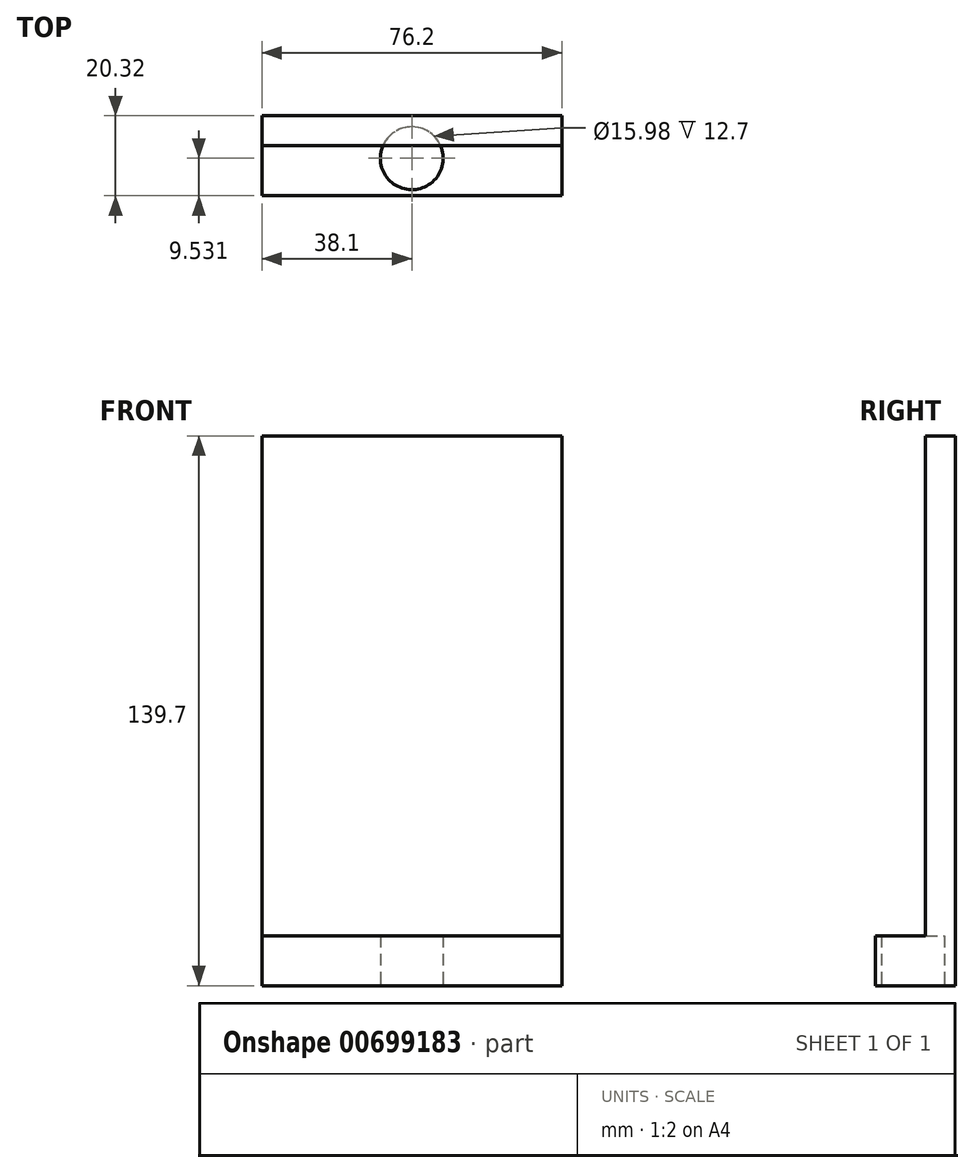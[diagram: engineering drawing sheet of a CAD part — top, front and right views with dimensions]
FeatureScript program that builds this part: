
annotation { "Feature Type Name" : "Feature", "Feature Type Description" : "" }
export const myFeature = defineFeature(function(context is Context, id is Id, definition is map)
    precondition{}
    {
        {
            var Q0;
            Q0=qCreatedBy(makeId("Front.planeOp"),FACE);
            var sketch = newSketch(context, id + "F0", { "sketchPlane" : qUnion([Q0])});
            skLineSegment(sketch, "E0.bottom", {"start": v(-38.1, 69.85) * mm, "end": v(38.1, 69.85) * mm});
            skLineSegment(sketch, "E0.top", {"start": v(-38.1, -69.85) * mm, "end": v(38.1, -69.85) * mm});
            skLineSegment(sketch, "E0.left", {"start": v(-38.1, 69.85) * mm, "end": v(-38.1, -69.85) * mm});
            skLineSegment(sketch, "E0.right", {"start": v(38.1, 69.85) * mm, "end": v(38.1, -69.85) * mm});
            skPoint(sketch, "E0.middle", {"position": v(0, 0) * mm});
            skSolve(sketch);
        }
        {
            var Q0;
            Q0 = qSketchRegion(id + "F0", true);
            extrude(context, id + "F1", {"entities" : qUnion([Q0]), "depth" : 7.62 * mm, "offsetDistance" : 25.4 * mm});
        }
        {
            var Q0;
            Q0=makeQuery(id+"F1.opExtrude","CAP_FACE",FACE,{"disambiguationData":[OSD([sQuery(id+"F0.wireOp",EDGE,"E0.bottom"),sQuery(id+"F0.wireOp",EDGE,"E0.top"),sQuery(id+"F0.wireOp",EDGE,"E0.left"),sQuery(id+"F0.wireOp",EDGE,"E0.right")])],"isStart":false});
            var sketch = newSketch(context, id + "F2", { "sketchPlane" : qUnion([Q0])});
            skLineSegment(sketch, "E1", {"start": v(-38.1, -57.15) * mm, "end": v(38.1, -57.15) * mm});
            skLineSegment(sketch, "E2", {"start": v(38.1, -57.15) * mm, "end": v(38.1, -69.85) * mm});
            skLineSegment(sketch, "E3", {"start": v(38.1, -69.85) * mm, "end": v(-38.1, -69.85) * mm});
            skLineSegment(sketch, "E4", {"start": v(-38.1, -69.85) * mm, "end": v(-38.1, -57.15) * mm});
            skSolve(sketch);
        }
        {
            var Q0;
            Q0 = qSketchRegion(id + "F2", true);
            extrude(context, id + "F3", {"entities" : qUnion([Q0]), "operationType" : NewBodyOperationType.ADD, "depth" : 12.7 * mm, "offsetDistance" : 25.4 * mm});
        }
        {
            var Q0;
            Q0=makeQuery(id+"F3.boolean.opBoolean","MERGE",FACE,{"derivedFrom":[makeQuery(id+"F1.opExtrude","SWEPT_FACE",FACE,{"disambiguationData":[OSD([sQuery(id+"F0.wireOp",EDGE,"E0.top")])]}),makeQuery(id+"F3.opExtrude","SWEPT_FACE",FACE,{"disambiguationData":[OSD([sQuery(id+"F2.wireOp",EDGE,"E3")])]})]});
            var sketch = newSketch(context, id + "F4", { "sketchPlane" : qUnion([Q0])});
            skCircle(sketch, "E5", {"center": v(0, 10.79) * mm, "radius": 7.99 * mm});
            skSolve(sketch);
        }
        {
            var Q0;
            Q0 = qSketchRegion(id + "F4", true);
            extrude(context, id + "F5", {"entities" : qUnion([Q0]), "operationType" : NewBodyOperationType.REMOVE, "oppositeDirection" : true, "depth" : 12.7 * mm, "offsetDistance" : 25.4 * mm});
        }
    });
